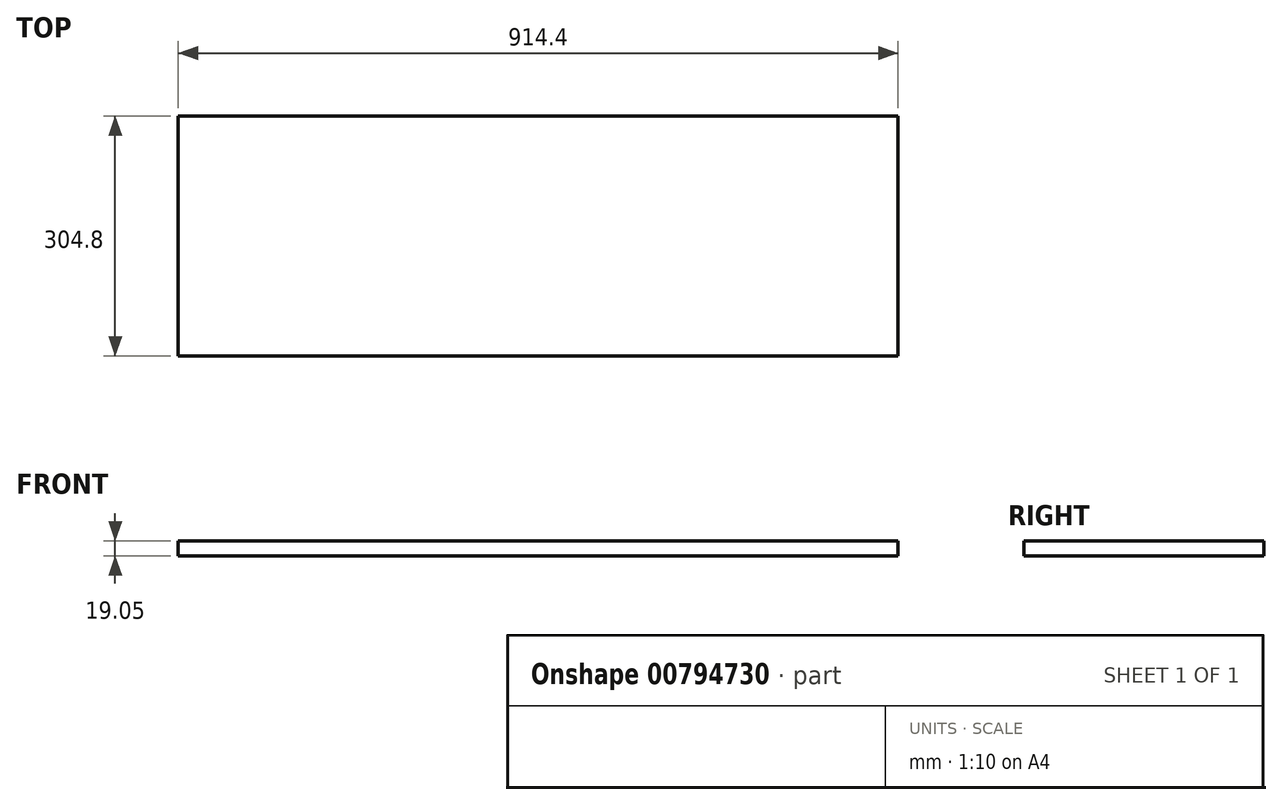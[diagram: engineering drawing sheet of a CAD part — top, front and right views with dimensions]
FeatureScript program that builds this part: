
annotation { "Feature Type Name" : "Feature", "Feature Type Description" : "" }
export const myFeature = defineFeature(function(context is Context, id is Id, definition is map)
    precondition{}
    {
        {
            var Q0;
            Q0=qCreatedBy(makeId("Top.planeOp"),FACE);
            var sketch = newSketch(context, id + "F0", { "sketchPlane" : qUnion([Q0])});
            skLineSegment(sketch, "E0.bottom", {"start": v(-61.53, 0) * mm, "end": v(852.87, 0) * mm});
            skLineSegment(sketch, "E0.top", {"start": v(-61.53, -304.8) * mm, "end": v(852.87, -304.8) * mm});
            skLineSegment(sketch, "E0.left", {"start": v(-61.53, 0) * mm, "end": v(-61.53, -304.8) * mm});
            skLineSegment(sketch, "E0.right", {"start": v(852.87, 0) * mm, "end": v(852.87, -304.8) * mm});
            skSolve(sketch);
        }
        {
            var Q0;
            Q0=makeQuery(id+"F0.imprint","IMPRINT",FACE,{"disambiguationData":[TD([[makeQuery(id+"F0.imprint","IMPRINT",EDGE,{"derivedFrom":sQuery(id+"F0.wireOp",EDGE,"E0.bottom")}),-1.0]])]});
            extrude(context, id + "F1", {"entities" : qUnion([Q0]), "depth" : 19.05 * mm, "offsetDistance" : 25.4 * mm});
        }
    });
